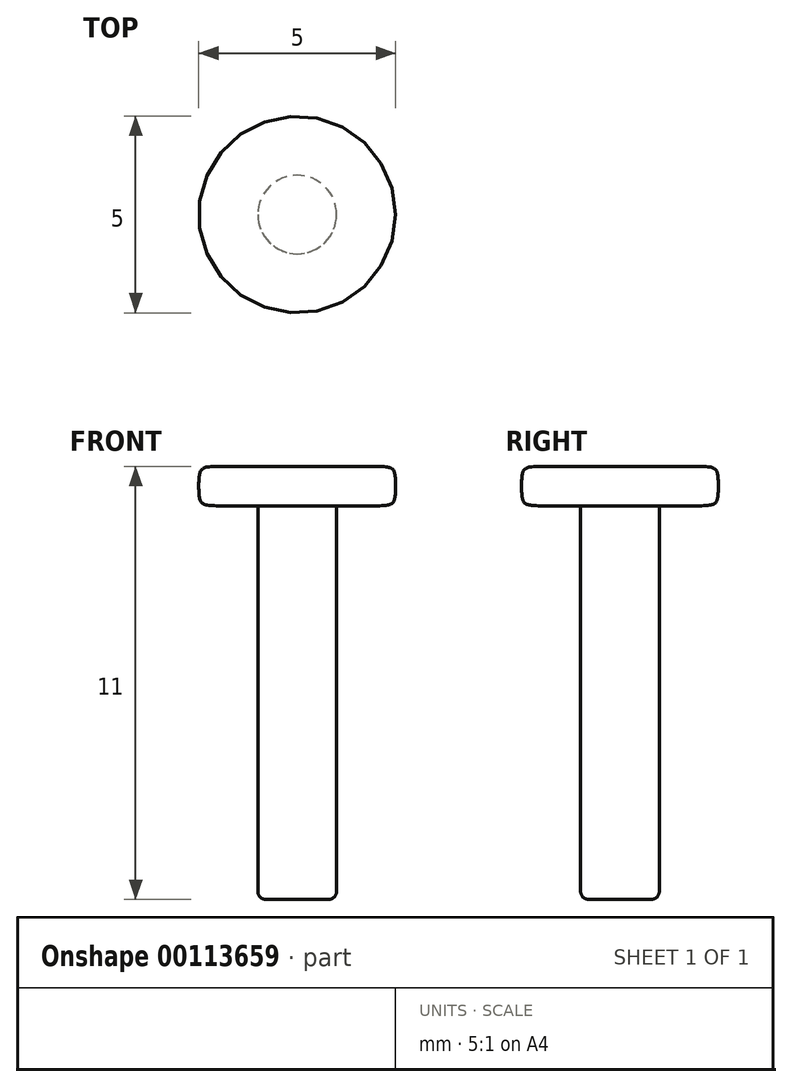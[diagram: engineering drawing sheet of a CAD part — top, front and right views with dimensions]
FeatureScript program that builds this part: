
annotation { "Feature Type Name" : "Feature", "Feature Type Description" : "" }
export const myFeature = defineFeature(function(context is Context, id is Id, definition is map)
    precondition{}
    {
        {
            var Q0;
            Q0=qCreatedBy(makeId("Top.planeOp"),FACE);
            var sketch = newSketch(context, id + "F0", { "sketchPlane" : qUnion([Q0])});
            skCircle(sketch, "E0", {"center": v(0, 0) * mm, "radius": 2.5 * mm});
            skSolve(sketch);
        }
        {
            var Q0;
            Q0=makeQuery(id+"F0.imprint","IMPRINT",FACE,{"disambiguationData":[TD([[makeQuery(id+"F0.imprint","IMPRINT",EDGE,{"derivedFrom":sQuery(id+"F0.wireOp",EDGE,"E0")}),1.0]])]});
            extrude(context, id + "F1", {"entities" : qUnion([Q0]), "oppositeDirection" : true, "depth" : 1 * mm});
        }
        {
            var Q0;
            Q0=makeQuery(id+"F1.opExtrude","CAP_EDGE",EDGE,{"disambiguationData":[OSD([sQuery(id+"F0.wireOp",EDGE,"E0")])],"isStart":true});
            var Q1;
            Q1=makeQuery(id+"F1.opExtrude","CAP_EDGE",EDGE,{"disambiguationData":[OSD([sQuery(id+"F0.wireOp",EDGE,"E0")])],"isStart":false});
            fillet(context, id + "F2", {"entities" : qUnion([Q0, Q1]), "radius" : 0.5 * mm, "tangentPropagation" : true, "rho" : 0.7, "crossSection" : FilletCrossSection.CONIC, "allowEdgeOverflow" : false});
        }
        {
            var Q0;
            Q0=makeQuery(id+"F1.opExtrude","CAP_FACE",FACE,{"disambiguationData":[OSD([sQuery(id+"F0.wireOp",EDGE,"E0")])],"isStart":false});
            var sketch = newSketch(context, id + "F3", { "sketchPlane" : qUnion([Q0])});
            skCircle(sketch, "E1", {"center": v(0, 0) * mm, "radius": 1 * mm});
            skSolve(sketch);
        }
        {
            var Q0;
            Q0=makeQuery(id+"F3.imprint","IMPRINT",FACE,{"disambiguationData":[TD([[makeQuery(id+"F3.imprint","IMPRINT",EDGE,{"derivedFrom":sQuery(id+"F3.wireOp",EDGE,"E1")}),1.0]])]});
            extrude(context, id + "F4", {"entities" : qUnion([Q0]), "operationType" : NewBodyOperationType.ADD, "depth" : 10 * mm});
        }
        {
            var Q0;
            Q0=makeQuery(id+"F4.opExtrude","CAP_EDGE",EDGE,{"disambiguationData":[OSD([sQuery(id+"F3.wireOp",EDGE,"E1")])],"isStart":true});
            var Q1;
            Q1=makeQuery(id+"F4.opExtrude","CAP_EDGE",EDGE,{"disambiguationData":[OSD([sQuery(id+"F3.wireOp",EDGE,"E1")])],"isStart":false});
            fillet(context, id + "F5", {"entities" : qUnion([Q0, Q1]), "radius" : 0.2 * mm, "tangentPropagation" : true, "allowEdgeOverflow" : false});
        }
    });
